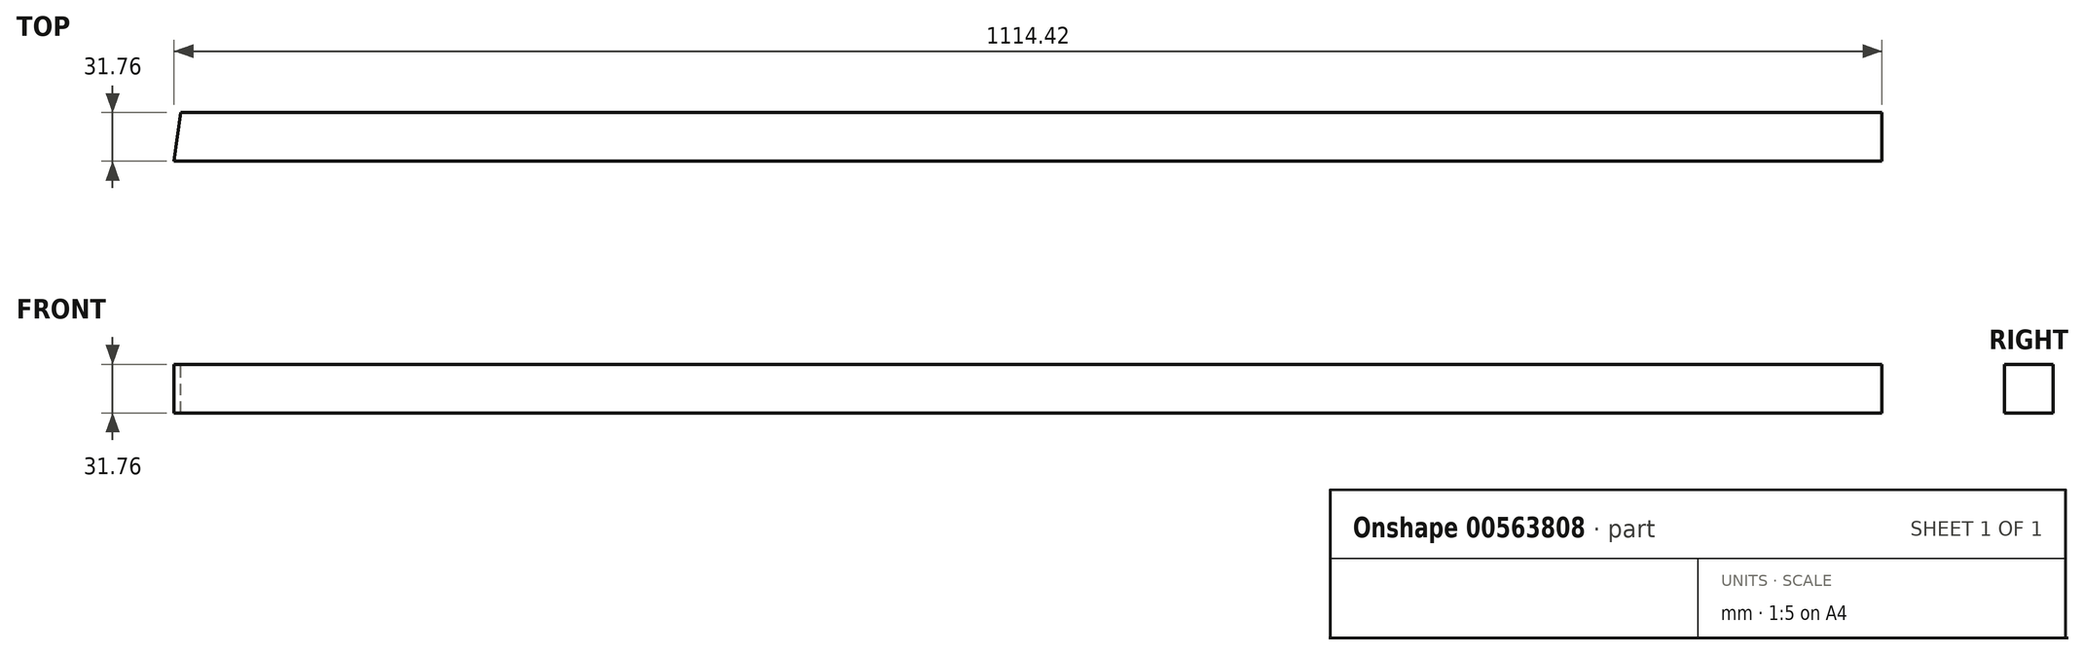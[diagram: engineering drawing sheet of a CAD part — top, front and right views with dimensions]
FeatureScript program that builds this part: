
annotation { "Feature Type Name" : "Feature", "Feature Type Description" : "" }
export const myFeature = defineFeature(function(context is Context, id is Id, definition is map)
    precondition{}
    {
        {
            var Q0;
            Q0=qCreatedBy(makeId("Top.planeOp"),FACE);
            var sketch = newSketch(context, id + "F0", { "sketchPlane" : qUnion([Q0])});
            skLineSegment(sketch, "E0.bottom", {"start": v(-557.21, 15.88) * mm, "end": v(557.21, 15.88) * mm});
            skLineSegment(sketch, "E0.top", {"start": v(-557.21, -15.88) * mm, "end": v(557.21, -15.88) * mm});
            skLineSegment(sketch, "E0.left", {"start": v(-557.21, 15.88) * mm, "end": v(-557.21, -15.88) * mm});
            skLineSegment(sketch, "E0.right", {"start": v(557.21, 15.88) * mm, "end": v(557.21, -15.88) * mm});
            skPoint(sketch, "E0.middle", {"position": v(0, 0) * mm});
            skSolve(sketch);
        }
        {
            var Q0;
            Q0=makeQuery(id+"F0.imprint","IMPRINT",FACE,{"disambiguationData":[TD([[makeQuery(id+"F0.imprint","IMPRINT",EDGE,{"derivedFrom":sQuery(id+"F0.wireOp",EDGE,"E0.bottom")}),-1.0]])]});
            extrude(context, id + "F1", {"entities" : qUnion([Q0]), "endBound" : BoundingType.SYMMETRIC, "depth" : 31.75 * mm, "offsetDistance" : 25.4 * mm});
        }
        {
            var Q0;
            Q0=makeQuery(id+"F1.opExtrude","CAP_FACE",FACE,{"disambiguationData":[OSD([sQuery(id+"F0.wireOp",EDGE,"E0.bottom"),sQuery(id+"F0.wireOp",EDGE,"E0.top"),sQuery(id+"F0.wireOp",EDGE,"E0.left"),sQuery(id+"F0.wireOp",EDGE,"E0.right")])],"isStart":false});
            var sketch = newSketch(context, id + "F2", { "sketchPlane" : qUnion([Q0])});
            skLineSegment(sketch, "E1", {"start": v(-557.21, -15.88) * mm, "end": v(-552.9, 15.88) * mm});
            skSolve(sketch);
        }
        {
            var Q0;
            {var subQ0=sQuery(id+"F2.wireOp",EDGE,"E1");Q0=makeQuery(id+"F2.imprint","IMPRINT",FACE,{"disambiguationData":[TD([[makeQuery(id+"F2.imprint","IMPRINT",EDGE,{"derivedFrom":subQ0}),1.0]])]});}
            extrude(context, id + "F3", {"entities" : qUnion([Q0]), "operationType" : NewBodyOperationType.REMOVE, "depth" : -31.75 * mm, "offsetDistance" : 25.4 * mm});
        }
    });
